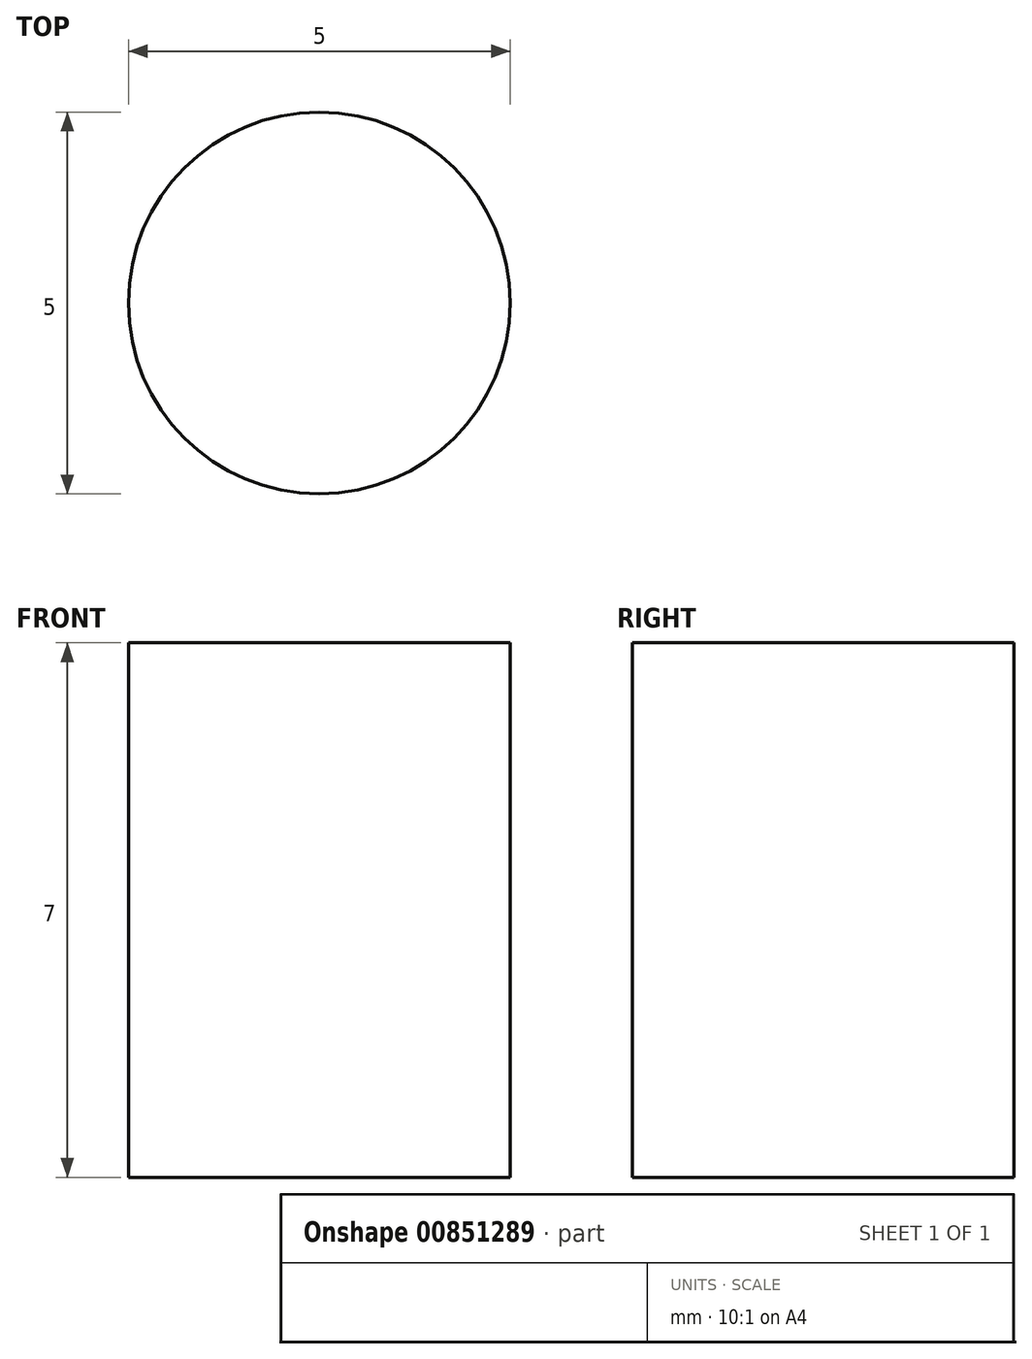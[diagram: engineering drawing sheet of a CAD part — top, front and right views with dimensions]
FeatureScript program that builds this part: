
annotation { "Feature Type Name" : "Feature", "Feature Type Description" : "" }
export const myFeature = defineFeature(function(context is Context, id is Id, definition is map)
    precondition{}
    {
        {
            var Q0;
            Q0=qCreatedBy(makeId("Top.planeOp"),FACE);
            var sketch = newSketch(context, id + "F0", { "sketchPlane" : qUnion([Q0])});
            skCircle(sketch, "E0", {"center": v(0, 0) * mm, "radius": 2.5 * mm});
            skSolve(sketch);
        }
        {
            var Q0;
            Q0=makeQuery(id+"F0.imprint","IMPRINT",FACE,{"disambiguationData":[TD([[makeQuery(id+"F0.imprint","IMPRINT",EDGE,{"derivedFrom":sQuery(id+"F0.wireOp",EDGE,"E0")}),1.0]])]});
            extrude(context, id + "F1", {"entities" : qUnion([Q0]), "depth" : 7 * mm, "offsetDistance" : 25 * mm});
        }
    });
